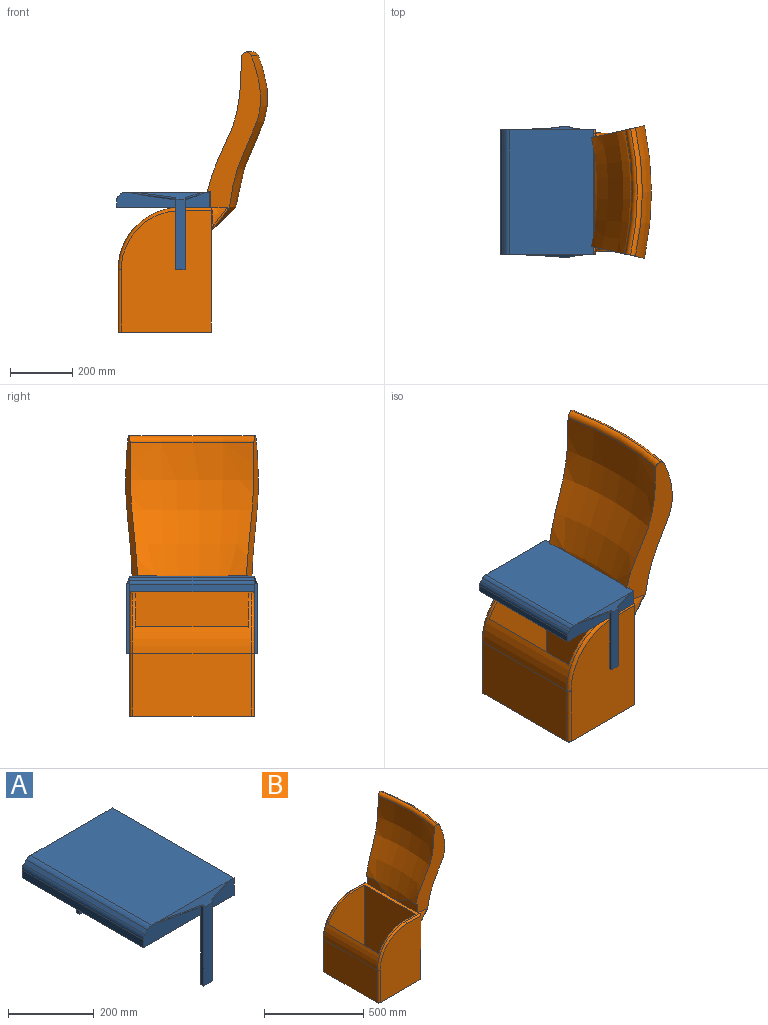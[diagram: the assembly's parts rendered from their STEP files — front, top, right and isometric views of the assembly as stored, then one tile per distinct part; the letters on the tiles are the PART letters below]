
ASSEMBLY  parts=2 mates=1
PART A: 31 faces, bbox 301.2x423.1x256.8 mm
  f0: plane 80x50mm, normal (0,-1,0), area 3110.5mm2, adj f3,f4,f5,f7,f12,f14
  f1: plane 190x50mm, normal (0,-1,0), area 7153.2mm2, adj f2,f3,f5,f8,f13,f15,f28,f29
  f2: plane 400x21.72mm, normal (-1,0,0), area 8686.3mm2, adj f1,f3,f17,f30
  f3: plane 400x300mm, normal (0,0,-1), area 120000mm2, adj f0,f1,f2,f4,f6,f16,f17,f18
  f4: plane 400x50mm, normal (1,0,0), area 20000mm2, adj f0,f3,f5,f16
  f5: plane 400x271.72mm, normal (0,0,1), area 108686.3mm2, adj f0,f1,f4,f11,f16,f17,f23,f29
  f6: plane 199.8x30mm, normal (0,1,0), area 5993.8mm2, adj f3,f7,f8,f9
  f7: plane 233.34x11.23mm, normal (1,0,0), area 2262.7mm2, adj f0,f6,f9,f10,f11,f12,f14
  f8: plane 232.3x10.57mm, normal (-1,0,0), area 2260.4mm2, adj f1,f6,f9,f10,f11,f13,f15
  f9: plane 30x10mm, normal (0,0,-1), area 300mm2, adj f6,f7,f8,f10
  f10: plane 225.61x30.01mm, normal (0,-1,0), area 6757.2mm2, adj f7,f8,f9,f11
  f11: bspline ~300x25mm, area 2682.6mm2, adj f5,f7,f8,f10,f14,f15
  f12: plane 21.77x6.75mm, normal (0.3,0,-0.96), area 31.5mm2, adj f0,f7,f14
  f13: plane 51.71x6.8mm, normal (-0.13,0,-0.99), area 73.3mm2, adj f1,f8,f15
  f14: bspline ~86.81x32.85mm, area 496.6mm2, adj f0,f7,f11,f12
  f15: bspline ~178.84x30.24mm, area 1150.2mm2, adj f1,f8,f11,f13
  f16: plane 80x50mm, normal (0,1,0), area 3110.5mm2, adj f3,f4,f5,f19,f24,f26
  f17: plane 190x50mm, normal (0,1,0), area 7153.2mm2, adj f2,f3,f5,f20,f25,f27,f28,f29
  f18: plane 199.8x30mm, normal (0,-1,0), area 5993.8mm2, adj f3,f19,f20,f21
  f19: plane 233.34x11.23mm, normal (1,0,0), area 2262.7mm2, adj f16,f18,f21,f22,f23,f24,f26
  f20: plane 232.3x10.57mm, normal (-1,0,0), area 2260.4mm2, adj f17,f18,f21,f22,f23,f25,f27
  f21: plane 30x10mm, normal (0,0,-1), area 300mm2, adj f18,f19,f20,f22
  f22: plane 225.61x30.01mm, normal (0,1,0), area 6757.2mm2, adj f19,f20,f21,f23
  f23: bspline ~300x25mm, area 2682.6mm2, adj f5,f19,f20,f22,f26,f27
  f24: plane 21.77x6.75mm, normal (0.3,0,-0.96), area 31.5mm2, adj f16,f19,f26
  f25: plane 51.71x6.8mm, normal (-0.13,0,-0.99), area 73.3mm2, adj f17,f20,f27
  f26: bspline ~86.81x32.85mm, area 496.6mm2, adj f16,f19,f23,f24
  f27: bspline ~178.84x30.24mm, area 1150.2mm2, adj f17,f20,f23,f25
  f28: plane 400x8.28mm, normal (-0.71,0,0.71), area 4686.3mm2, adj f1,f17,f29,f30
  f29: cylinder r=20mm len=400mm, axis (0,-1,0), area 6283.2mm2, adj f1,f5,f17,f28
  f30: cylinder r=20mm len=400mm, axis (0,-1,0), area 6283.2mm2, adj f1,f2,f17,f28
PART B: 41 faces, bbox 567.2x467.4x920 mm
  f0: revolved ~479.94x398.32mm, area 177889.5mm2, adj f2,f4,f5,f6,f7,f8,f27
  f1: plane 357.7x3.95mm, normal (0,0,-1), area 1410.4mm2, adj f2,f4,f9,f24
  f2: plane 535.6x192.13mm, normal (-0.22,-0.98,0), area 33565.2mm2, adj f0,f1,f3,f7,f8,f10,f21,f22
  f3: revolved ~480.24x425.76mm, area 206500.8mm2, adj f2,f4,f25,f26
  f4: plane 536.17x192.11mm, normal (-0.22,0.98,0), area 33565.8mm2, adj f0,f1,f3,f5,f6,f10,f22,f23
  f5: plane 58.58x10.4mm, normal (0,0,-1), area 285.4mm2, adj f0,f4,f6
  f6: plane 197.39x72.02mm, normal (-1,0,0), area 5382.8mm2, adj f0,f4,f5,f10
  f7: plane 197.38x72.02mm, normal (-1,0,0), area 5382.8mm2, adj f0,f2,f8,f10
  f8: plane 58.58x10.4mm, normal (0,0,-1), area 285.4mm2, adj f0,f2,f7
  f9: plane 400x400mm, normal (1,0,0), area 131643.9mm2, adj f1,f10,f12,f14,f15,f24,f30,f33
  f10: plane 380x100mm, normal (0,0,1), area 8210.3mm2, adj f2,f4,f6,f7,f9,f11,f16,f17
  f11: cylinder r=200mm len=380mm, axis (0,1,0), area 38757.1mm2, adj f10,f13,f16,f17,f18,f29,f32
  f12: plane 400x300mm, normal (0,0,-1), area 119957.1mm2, adj f9,f13,f14,f15,f28,f31
  f13: plane 380x200mm, normal (-1,0,0), area 76000mm2, adj f11,f12,f28,f31
  f14: plane 390x290mm, normal (0,-1,0), area 105352.9mm2, adj f9,f12,f31,f32,f33
  f15: plane 390x290mm, normal (0,1,0), area 105352.9mm2, adj f9,f12,f28,f29,f30
  f16: plane 380x260mm, normal (0,1,0), area 93041.4mm2, adj f10,f11,f18,f19,f20
  f17: plane 380x260mm, normal (0,-1,0), area 93041.4mm2, adj f10,f11,f18,f19,f20
  f18: plane 360x267.18mm, normal (1,0,0), area 96184.1mm2, adj f11,f16,f17,f20
  f19: plane 380x360mm, normal (-1,0,0), area 136800mm2, adj f10,f16,f17,f20
  f20: plane 360x260mm, normal (0,0,1), area 93600mm2, adj f16,f17,f18,f19
  f21: bspline ~73.84x58.05mm, area 1611.6mm2, adj f2,f24,f34,f35
  f22: bspline ~381.75x78.95mm, area 34938.7mm2, adj f2,f4,f25,f35,f37,f38
  f23: bspline ~73.84x58.05mm, area 1605.7mm2, adj f4,f24,f38,f40
  f24: plane 383.43x4.08mm, normal (-0.6,0,0.8), area 1834.8mm2, adj f1,f9,f21,f23,f34,f40
  f25: bspline ~387.15x26.83mm, area 6331.5mm2, adj f2,f3,f4,f22
  f26: torus R=934.85mm, axis (0,0,-1), area 8834.9mm2, adj f2,f3,f4,f27
  f27: torus R=940.16mm, axis (0,0,-1), area 11644.3mm2, adj f0,f2,f4,f26
  f28: cylinder r=10mm len=200mm, axis (0,0,-1), area 3141.6mm2, adj f12,f13,f15,f29
  f29: torus R=190mm, axis (0,-1,0), area 4845.1mm2, adj f11,f15,f28,f30
  f30: cylinder r=10mm len=100mm, axis (-1,0,0), area 1570.8mm2, adj f9,f10,f15,f29
  f31: cylinder r=10mm len=200mm, axis (0,0,1), area 3141.6mm2, adj f12,f13,f14,f32
  f32: torus R=190mm, axis (0,-1,0), area 4845.1mm2, adj f11,f14,f31,f33
  f33: cylinder r=10mm len=100mm, axis (1,0,0), area 1570.8mm2, adj f9,f10,f14,f32
  f34: bspline ~61.68x6.83mm, area 368.8mm2, adj f9,f21,f24,f36
  f35: bspline ~92.38x74.3mm, area 515mm2, adj f2,f21,f22,f36
  f36: bspline ~17.96x11.42mm, area 93.8mm2, adj f9,f34,f35,f37
  f37: bspline ~401.09x3.65mm, area 1437.5mm2, adj f9,f22,f36,f39
  f38: bspline ~92.18x74.17mm, area 512.1mm2, adj f4,f22,f23,f39
  f39: bspline ~18.98x10.62mm, area 94.4mm2, adj f9,f37,f38,f40
  f40: bspline ~61.19x6.85mm, area 371.3mm2, adj f9,f23,f24,f39
PLACE A rot(axis=(0,1,-0.01),0deg) t=(-36.71,-23.46,26.25)mm
PLACE B t=(277.41,-23.46,43.35)mm fixed
MATE revolute A.f6 <-> B.f11  axis (0,1,0) through (180.2,-223.46,-156.65)mm
